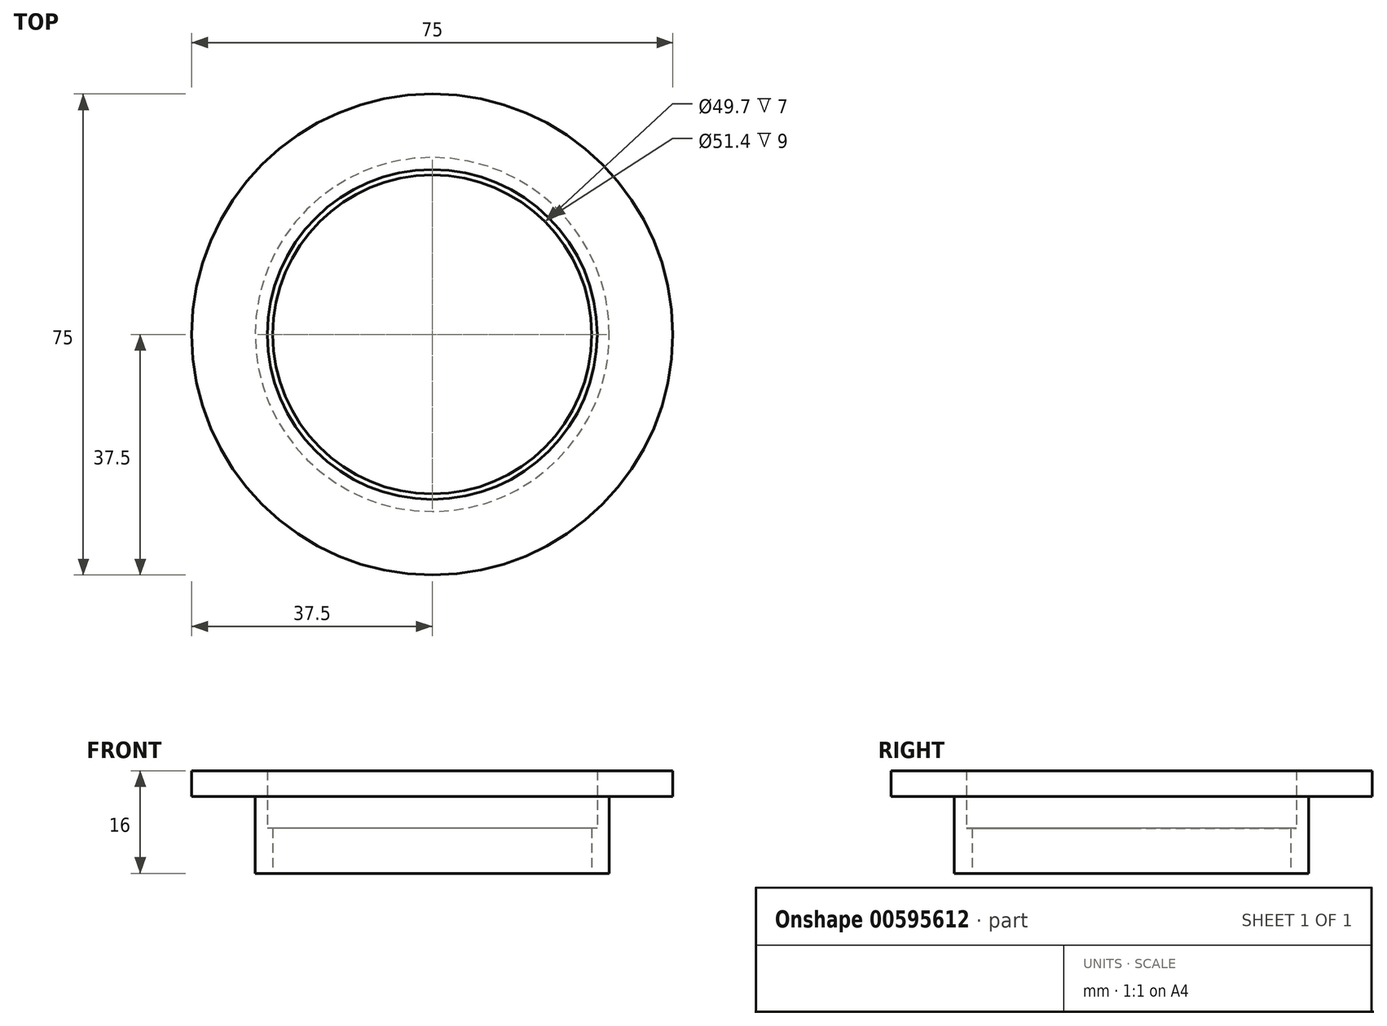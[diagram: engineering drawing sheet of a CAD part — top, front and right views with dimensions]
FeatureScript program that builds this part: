
annotation { "Feature Type Name" : "Feature", "Feature Type Description" : "" }
export const myFeature = defineFeature(function(context is Context, id is Id, definition is map)
    precondition{}
    {
        {
            var Q0;
            Q0=qCreatedBy(makeId("Top.planeOp"),FACE);
            var sketch = newSketch(context, id + "F0", { "sketchPlane" : qUnion([Q0])});
            skCircle(sketch, "E0", {"center": v(0, 0) * mm, "radius": 24.85 * mm});
            skCircle(sketch, "E1", {"center": v(0, 0) * mm, "radius": 25.7 * mm});
            skSolve(sketch);
        }
        {
            var Q0;
            Q0=qSketchRegion(id+"F0",true);
            extrude(context, id + "F1", {"entities" : qUnion([Q0]), "depth" : 7 * mm, "offsetDistance" : 25 * mm});
        }
        {
            var Q0;
            Q0=qCreatedBy(makeId("Top.planeOp"),FACE);
            var sketch = newSketch(context, id + "F2", { "sketchPlane" : qUnion([Q0])});
            skCircle(sketch, "E2", {"center": v(0, 0) * mm, "radius": 25.7 * mm});
            skCircle(sketch, "E3", {"center": v(0, 0) * mm, "radius": 27.6 * mm});
            skSolve(sketch);
        }
        {
            var Q0;
            Q0=qSketchRegion(id+"F2",true);
            extrude(context, id + "F3", {"entities" : qUnion([Q0]), "operationType" : NewBodyOperationType.ADD, "depth" : 12 * mm, "offsetDistance" : 25 * mm});
        }
        {
            var Q0;
            Q0=qCreatedBy(makeId("Top.planeOp"),FACE);
            cPlane(context, id + "F4", {"entities" : qUnion([Q0]), "cplaneType" : CPlaneType.OFFSET, "offset" : 12 * mm, "width" : 150 * mm, "height" : 150 * mm});
        }
        {
            var Q0;
            Q0=qCreatedBy(id+"F4.planeOp",FACE);
            var sketch = newSketch(context, id + "F5", { "sketchPlane" : qUnion([Q0])});
            skCircle(sketch, "E4", {"center": v(0, 0) * mm, "radius": 37.5 * mm});
            skCircle(sketch, "E5", {"center": v(0, 0) * mm, "radius": 25.7 * mm});
            skSolve(sketch);
        }
        {
            var Q0;
            Q0=qSketchRegion(id+"F5",true);
            extrude(context, id + "F6", {"entities" : qUnion([Q0]), "operationType" : NewBodyOperationType.ADD, "depth" : 4 * mm, "offsetDistance" : 25 * mm});
        }
    });
